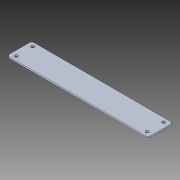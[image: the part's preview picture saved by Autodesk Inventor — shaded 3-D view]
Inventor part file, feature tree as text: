
AUTODESK INVENTOR PART (.ipt)
format: ipt  version: 2018 (Build 220112000, 112)  size: 82,944 bytes
history: native  units: in
note: dims shown in document units (in); Inventor stores cm internally (conversion verified against a paired STEP export)
features: chamfer x1
ambient origin geometry x8: Origin, YZ Plane, XZ Plane, XY Plane, X Axis, Y Axis, Z Axis, Center Point
bodies: Solid1 (feature_tree)
feature tree (1):
  chamfer  "Chamfer1"  [1 undecoded]
note: 1 required parameter value undecoded (feature->parameter linkage not recoverable at this tier; creation-order binding heuristic only, values carry confidence <= 0.55)
